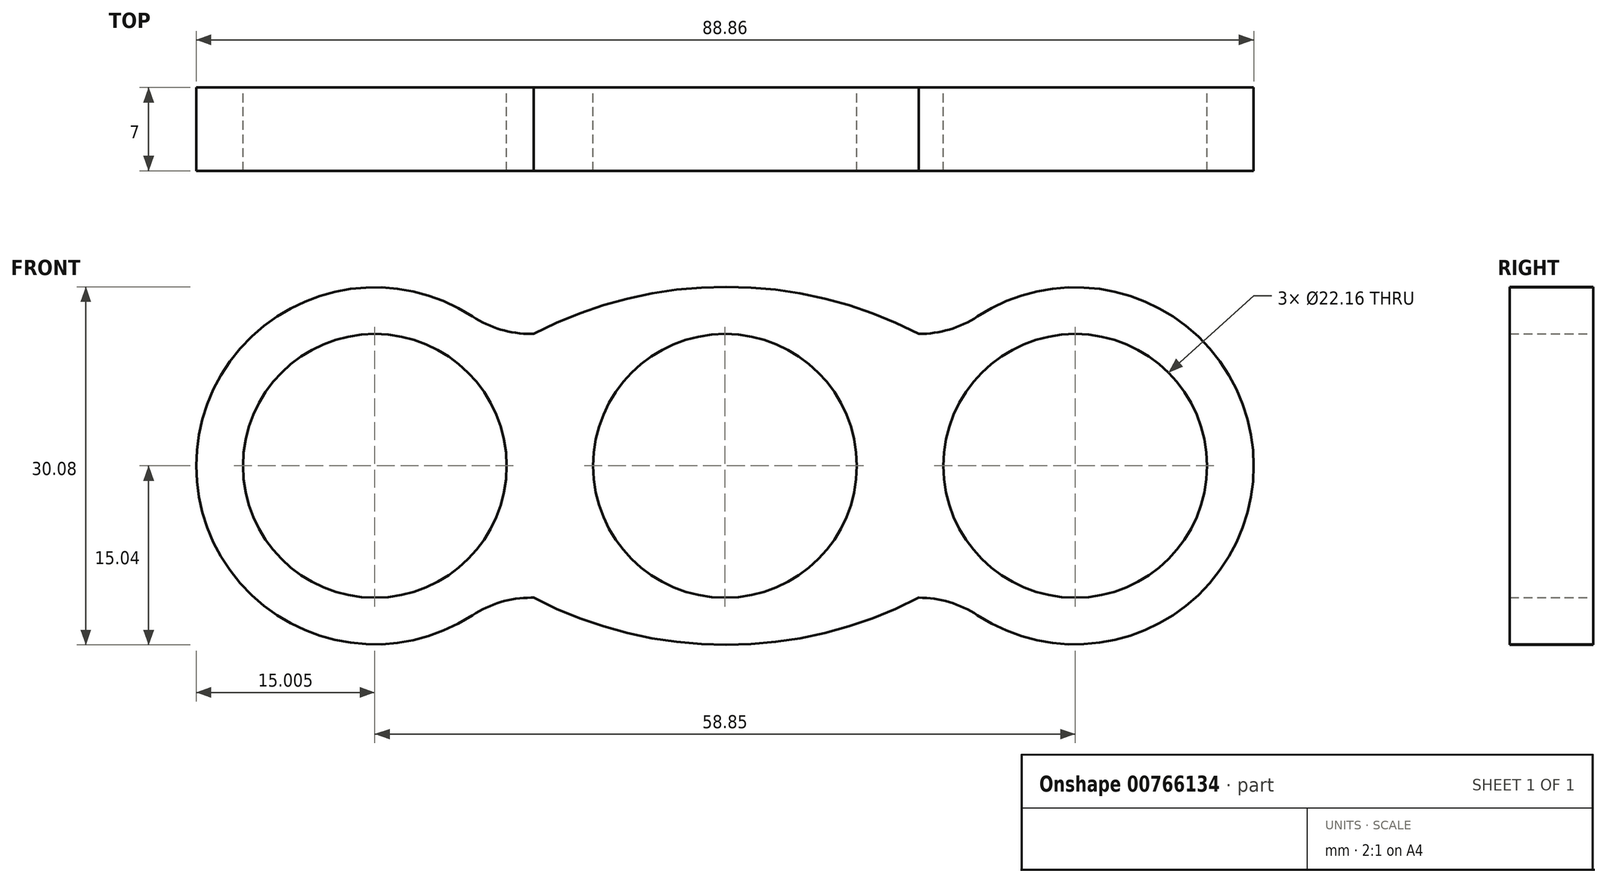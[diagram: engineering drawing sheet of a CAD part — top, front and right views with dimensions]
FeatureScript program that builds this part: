
annotation { "Feature Type Name" : "Feature", "Feature Type Description" : "" }
export const myFeature = defineFeature(function(context is Context, id is Id, definition is map)
    precondition{}
    {
        {
            var Q0;
            Q0=qCreatedBy(makeId("Front.planeOp"),FACE);
            var sketch = newSketch(context, id + "F0", { "sketchPlane" : qUnion([Q0])});
            skCircle(sketch, "E0", {"center": v(0, 0) * mm, "radius": 11.08 * mm});
            skLineSegment(sketch, "E1", {"start": v(16.08, 11.08) * mm, "end": v(16.28, 11.08) * mm});
            skLineSegment(sketch, "E2", {"start": v(16.08, -11.08) * mm, "end": v(16.28, -11.08) * mm});
            skLineSegment(sketch, "E3", {"start": v(-16.08, 11.08) * mm, "end": v(-16.28, 11.08) * mm});
            skLineSegment(sketch, "E4", {"start": v(-16.08, -11.08) * mm, "end": v(-16.28, -11.08) * mm});
            skLineSegment(sketch, "E5", {"start": v(-11.08, 16.08) * mm, "end": v(-11.08, 16.28) * mm});
            skLineSegment(sketch, "E6", {"start": v(11.08, 16.08) * mm, "end": v(11.08, 16.28) * mm});
            skLineSegment(sketch, "E7", {"start": v(11.08, -16.08) * mm, "end": v(11.08, -16.28) * mm});
            skCircle(sketch, "E8", {"center": v(-29.43, 0) * mm, "radius": 11.08 * mm});
            skCircle(sketch, "E9", {"center": v(29.43, 0) * mm, "radius": 11.08 * mm});
            skPoint(sketch, "E10.orphan", {"position": v(0, 11.08) * mm});
            skPoint(sketch, "E11.orphan", {"position": v(11.08, 0) * mm});
            skPoint(sketch, "E12.orphan", {"position": v(0, -11.08) * mm});
            skPoint(sketch, "E13.orphan", {"position": v(-11.08, 0) * mm});
            skPoint(sketch, "E14.visualSharp", {"position": v(-11.08, 11.08) * mm});
            skPoint(sketch, "E15.visualSharp", {"position": v(11.08, 11.08) * mm});
            skPoint(sketch, "E16.visualSharp", {"position": v(11.08, -11.08) * mm});
            skPoint(sketch, "E17.visualSharp", {"position": v(-11.08, -11.08) * mm});
            skArc(sketch, "E18", {"start": v(-21.2, 12.55) * mm, "mid": v(-44.43, 0) * mm, "end": v(-21.2, -12.55) * mm});
            skArc(sketch, "E19", {"start": v(21.2, -12.55) * mm, "mid": v(44.43, 0) * mm, "end": v(21.2, 12.55) * mm});
            skPoint(sketch, "E20.visualSharp", {"position": v(19.31, 11.08) * mm});
            skArc(sketch, "E20.filletArc", {"start": v(16.28, 11.08) * mm, "mid": v(18.85, 11.46) * mm, "end": v(21.2, 12.55) * mm});
            skPoint(sketch, "E21.visualSharp", {"position": v(19.31, -11.08) * mm});
            skArc(sketch, "E21.filletArc", {"start": v(21.2, -12.55) * mm, "mid": v(18.85, -11.46) * mm, "end": v(16.28, -11.08) * mm});
            skPoint(sketch, "E22.visualSharp", {"position": v(-19.31, -11.08) * mm});
            skArc(sketch, "E22.filletArc", {"start": v(-16.28, -11.08) * mm, "mid": v(-18.85, -11.46) * mm, "end": v(-21.2, -12.55) * mm});
            skPoint(sketch, "E23.visualSharp", {"position": v(-19.31, 11.08) * mm});
            skArc(sketch, "E23.filletArc", {"start": v(-21.2, 12.55) * mm, "mid": v(-18.85, 11.46) * mm, "end": v(-16.28, 11.08) * mm});
            skArc(sketch, "E24", {"start": v(16.28, 11.08) * mm, "mid": v(0.1, 15.04) * mm, "end": v(-16.08, 11.08) * mm});
            skArc(sketch, "E25", {"start": v(-16.08, -11.08) * mm, "mid": v(0.1, -15.04) * mm, "end": v(16.28, -11.08) * mm});
            skSolve(sketch);
        }
        {
            var Q0;
            Q0 = qSketchRegion(id + "F0", true);
            extrude(context, id + "F1", {"entities" : qUnion([Q0]), "depth" : 7 * mm, "offsetDistance" : 25 * mm});
        }
    });
